# Revit family: 101651001_Sanitario Power One Blanco
name_source: partatom
category: Generic Models
units: mm (PartAtom-declared; Revit-internal decimal feet)

## family parameters
Always vertical = Yes
Can host rebar = No
Cut with Voids When Loaded = No
Part Type = Normal
Room Calculation Point = No
Round Connector Dimension = Use Diameter
Shared = No
Work Plane-Based = No

## types (1)
- 101651001_Sanitario Power One Blanco
    Acabado = Brillante
    Alto = 72 cm
    Altura de la taza = 41 cm
    Ancho = 38 cm
    Capacidad de descarga = 600 g
    Colección = Burgos
    Consumo de agua = 4.8 lt
    Creado por = IDD
    Description = Este sanitario te ofrece un diseño moderno y desempeño de alta eficiencia. Con sistema de accionamiento con botón single y sistema jet. Tiene asiento de cierre suave y la altura ideal para mayor comodidad. ¡Justo lo que buscabas!
    Fecha de creación = 6/08/2020
    Garantía = Garantia completa para siempre en la porcelana
    Garantías de otros componentes = 5 años en grifería tanque y asiento.
    Largo = 69 cm
    Línea = Burgos
    MATERIAL = Corona_Porcelana_Sanitaria
    Materiales = Porcelana sanitaria
    Perfil de la taza = Alongado
    Sistema de descarga = Botón dual azul Corona
    Tecnologías = MaxiClean
    Tipo de asiento = Cierre lento
    Tipo de instalación = A piso
    URL = https://corona.co
    Uso = Residencial

## geometry (parser evidence)
native form markers: Sweep x14
no freeform markers — native parametric forms only
